# Revit family: KDW010113
name_source: partatom
category: Plumbing Fixtures
revit_build: Autodesk Revit 2015 (Build: 20140606_1530(x64)
units: mm (PartAtom-declared; Revit-internal decimal feet)

## types (1)
- PURO WANDWASCHTISCH 3162 300x550
    Accessoire = Yes
    Color = https://www.kaldewei.co.uk
    ColourOptions = https://www.kaldewei.co.uk
    Durability = https://www.kaldewei.de
    Features = https://www.kaldewei.co.uk
    Finish = https://n
    Finition = Kaldewei
    HasGrabHandles = https://www.kaldewei.co.uk
    IfcExportAs = WASHHANDBASIN
    IfcExportType = IfcSanitaryTerminalType
    IntegralAccessories = https://www.kaldewei.co.uk
    Manufacturer = Kaldewei
    ManufacturerCountry = GERMANY
    ManufacturerName = KALDEWEI
    ManufacturerURL = https://www.kaldewei.com
    Material = steel enamel
    Metal = Acier, chromé
    Model = PUROWANDWASCHTISCH
    Name = PUROWANDWASCHTISCH
    NominalHeight = 100 mm
    NominalLength = 550
    NominalWidth = 300
    ObjectName = PURO Wall-hung washbasin 300x550
    ObjectNorm = EN 14688EU DECLARATION OF PERFORMANCE(https://www.kaldewei.de
    ObjectPicture = https://www.kaldewei.co.uk
    ObjectURL = https://www.kaldewei.co.uk
    Polantis code = KDW010113
    ProductInformation = Model No.3162: - elegant rectangular washbasin in a classically minimalist design- reduced precise edges- very generous interior dimensions- clean and timeless lines – immortalised in long-lasting KALDEWEI steel enamel- harmonises perfectly with the Puro bath series- designed by Anke Salomon
    Revision = 1
    SerialNumber = 3162
    Shape = Wall-Hung,Handbasin
    Size = 300x550
    SupportFrame = https://www.kaldewei.co.uk
    Sustainability = https://kaldewei-fa.secure.footprint.net
    TechnicalDataURL = https://kaldewei.typo-live.web-factory.de
    Type Comments = PURO WANDWASCHTISCH 3162 300x550
    UNSPSCCode = 30181504
    UNSPSCNames = Sinks
    URL = https://www.kaldewei.co.uk
    Uniclass 2015 = Pr_40_20_96
    Version = 4
    WarrantyDurationParts = 30
    WarrantyDurationUnit = Year
    WarrantyStartDate = https://www.kaldewei.co.uk
    Weight = 10,2

## geometry (parser evidence)
native form markers: Sweep x7
no freeform markers — native parametric forms only
